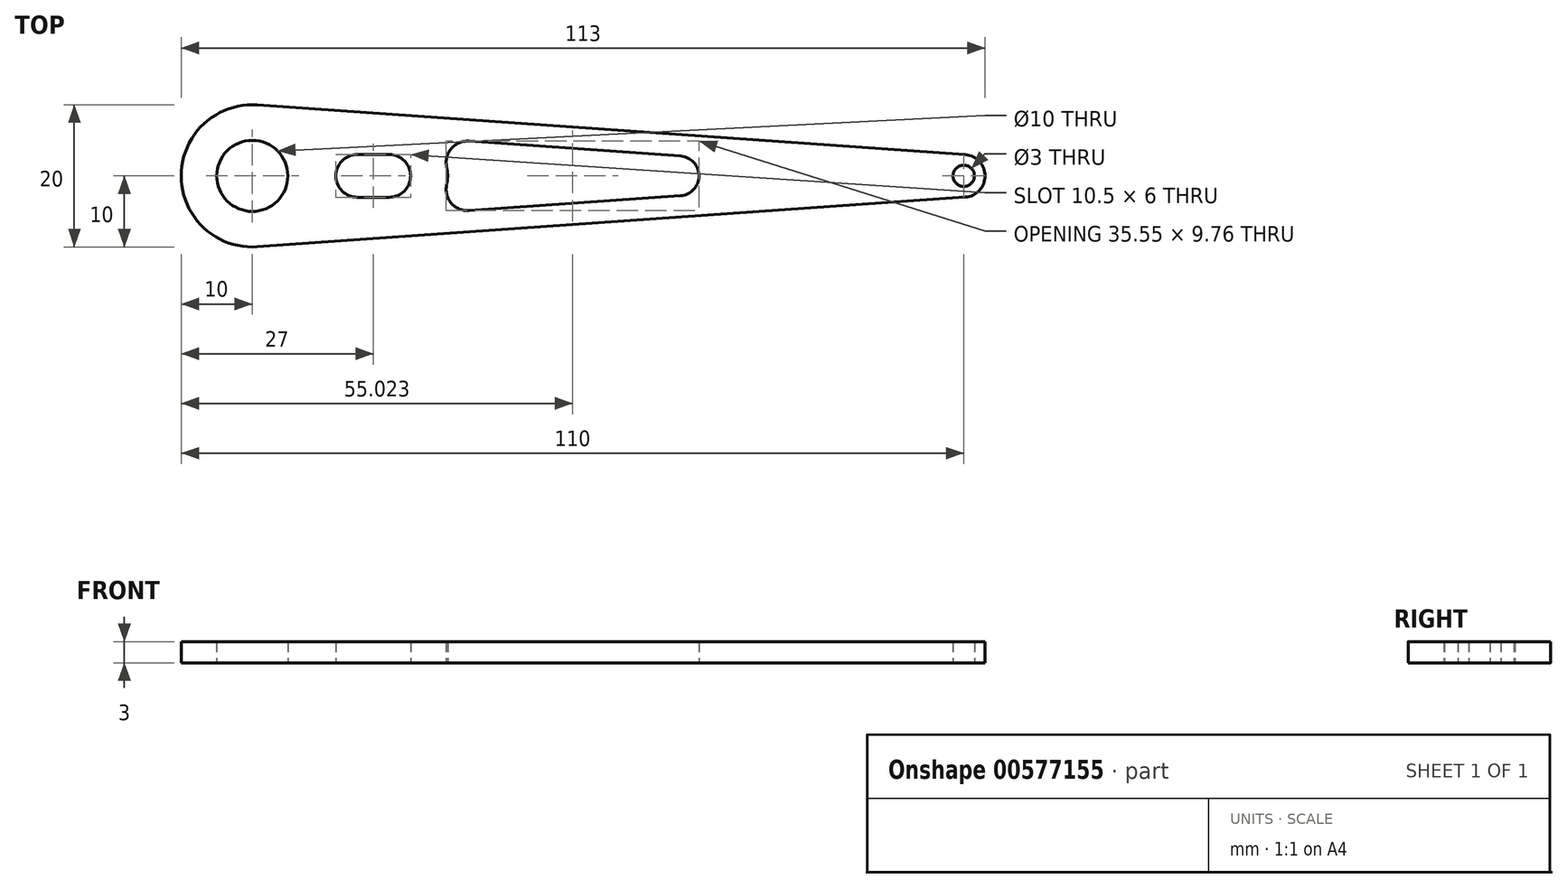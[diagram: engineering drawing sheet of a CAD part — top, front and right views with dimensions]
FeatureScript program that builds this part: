
annotation { "Feature Type Name" : "Feature", "Feature Type Description" : "" }
export const myFeature = defineFeature(function(context is Context, id is Id, definition is map)
    precondition{}
    {
        {
            var Q0;
            Q0=qCreatedBy(makeId("Top.planeOp"),FACE);
            var sketch = newSketch(context, id + "F0", { "sketchPlane" : qUnion([Q0])});
            skArc(sketch, "E0", {"start": v(-49.3, 9.98) * mm, "mid": v(-60, 0) * mm, "end": v(-49.3, -9.98) * mm});
            skArc(sketch, "E1", {"start": v(50.2, -3) * mm, "mid": v(53, 0) * mm, "end": v(50.2, 3) * mm});
            skLineSegment(sketch, "E2", {"start": v(-49.3, 9.98) * mm, "end": v(50.21, 3) * mm});
            skLineSegment(sketch, "E3", {"start": v(-49.3, -9.98) * mm, "end": v(50.21, -3) * mm});
            skCircle(sketch, "E4", {"center": v(50, 0) * mm, "radius": 1.5 * mm});
            skArc(sketch, "E5", {"start": v(-22.68, -1.22) * mm, "mid": v(-22.54, 0) * mm, "end": v(-22.68, 1.22) * mm});
            skArc(sketch, "E6", {"start": v(10.2, -2.8) * mm, "mid": v(12.8, 0) * mm, "end": v(10.2, 2.8) * mm});
            skLineSegment(sketch, "E7", {"start": v(-19.54, 4.88) * mm, "end": v(10.2, 2.8) * mm});
            skLineSegment(sketch, "E8", {"start": v(-19.54, -4.88) * mm, "end": v(10.2, -2.8) * mm});
            skPoint(sketch, "E9.visualSharp", {"position": v(-27.62, 5.45) * mm});
            skArc(sketch, "E9.filletArc", {"start": v(-19.54, 4.88) * mm, "mid": v(-22.03, 3.84) * mm, "end": v(-22.68, 1.22) * mm});
            skPoint(sketch, "E10.visualSharp", {"position": v(-27.62, -5.45) * mm});
            skArc(sketch, "E10.filletArc", {"start": v(-22.68, -1.22) * mm, "mid": v(-22.03, -3.84) * mm, "end": v(-19.54, -4.88) * mm});
            skCircle(sketch, "E11", {"center": v(-50, 0) * mm, "radius": 5 * mm});
            skArc(sketch, "E12", {"start": v(-35.25, 3) * mm, "mid": v(-38.25, 0) * mm, "end": v(-35.25, -3) * mm});
            skLineSegment(sketch, "E13", {"start": v(-35.25, -3) * mm, "end": v(-30.75, -3) * mm});
            skArc(sketch, "E14", {"start": v(-30.75, -3) * mm, "mid": v(-27.75, 0) * mm, "end": v(-30.75, 3) * mm});
            skLineSegment(sketch, "E15", {"start": v(-35.25, 3) * mm, "end": v(-30.75, 3) * mm});
            skSolve(sketch);
        }
        {
            var Q0;
            Q0=qSketchRegion(id+"F0",true);
            extrude(context, id + "F1", {"entities" : qUnion([Q0]), "endBound" : BoundingType.SYMMETRIC, "depth" : 3 * mm});
        }
    });
